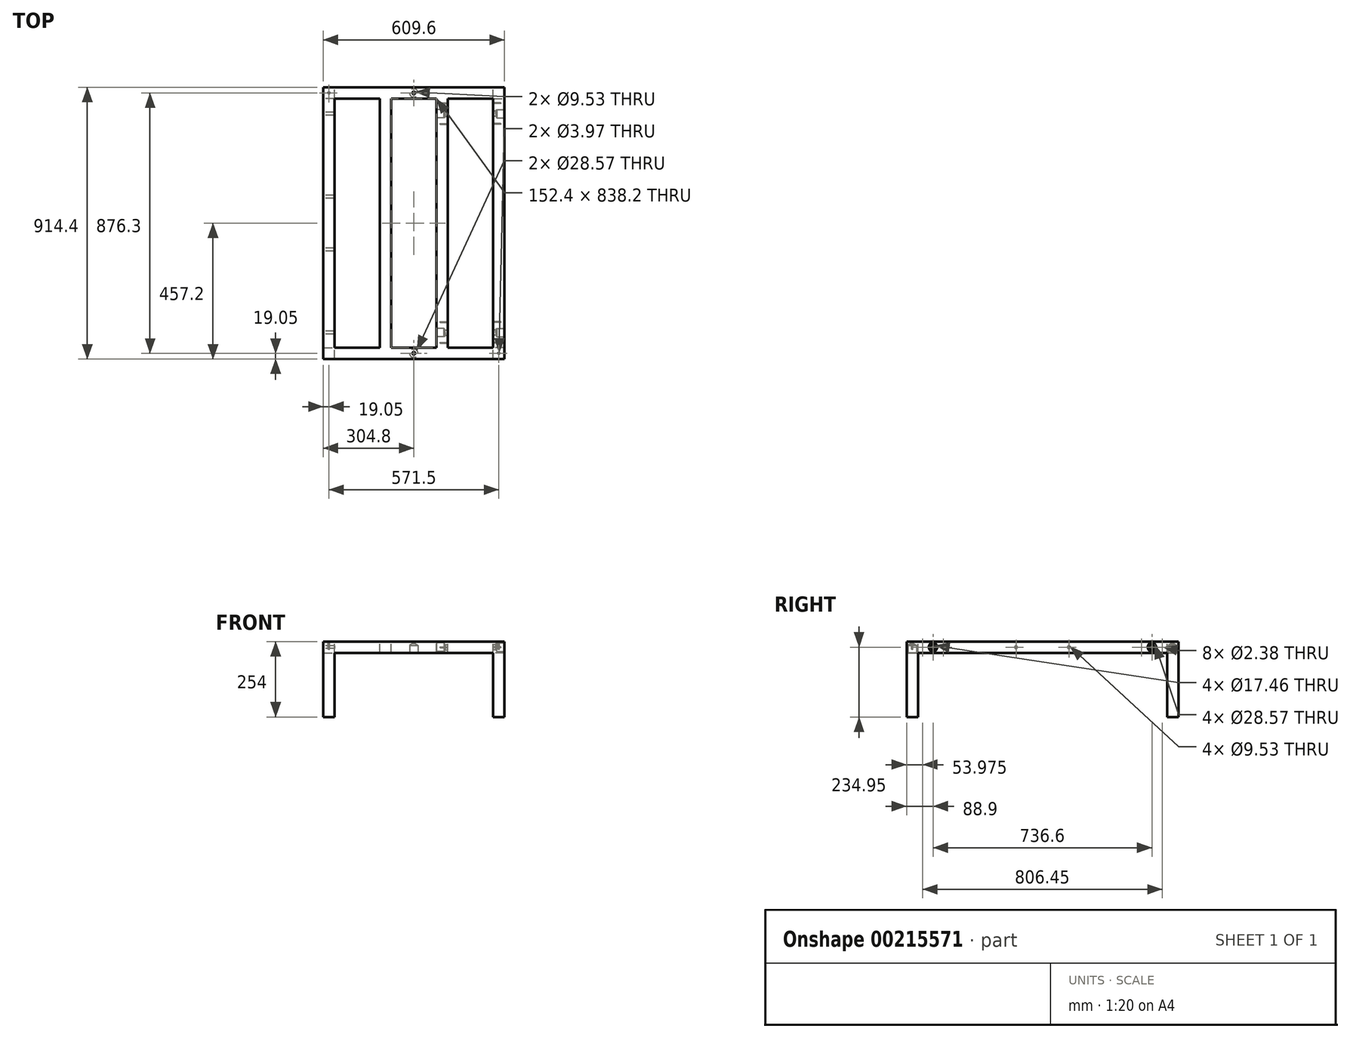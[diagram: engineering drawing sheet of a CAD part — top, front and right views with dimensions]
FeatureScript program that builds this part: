
annotation { "Feature Type Name" : "Feature", "Feature Type Description" : "" }
export const myFeature = defineFeature(function(context is Context, id is Id, definition is map)
    precondition{}
    {
        {
            var Q0;
            Q0=qCreatedBy(makeId("Top.planeOp"),FACE);
            var sketch = newSketch(context, id + "F0", { "sketchPlane" : qUnion([Q0])});
            skLineSegment(sketch, "E0.bottom", {"start": v(304.8, 457.2) * mm, "end": v(-304.8, 457.2) * mm});
            skLineSegment(sketch, "E0.top", {"start": v(304.8, -457.2) * mm, "end": v(-304.8, -457.2) * mm});
            skLineSegment(sketch, "E0.left", {"start": v(304.8, 457.2) * mm, "end": v(304.8, -457.2) * mm});
            skLineSegment(sketch, "E0.right", {"start": v(-304.8, 457.2) * mm, "end": v(-304.8, -457.2) * mm});
            skPoint(sketch, "E0.middle", {"position": v(0, 0) * mm});
            skLineSegment(sketch, "E1.bottom", {"start": v(266.7, 419.1) * mm, "end": v(114.3, 419.1) * mm});
            skLineSegment(sketch, "E1.top", {"start": v(266.7, -419.1) * mm, "end": v(114.3, -419.1) * mm});
            skLineSegment(sketch, "E1.left", {"start": v(266.7, 419.1) * mm, "end": v(266.7, -419.1) * mm});
            skLineSegment(sketch, "E1.right", {"start": v(-266.7, 419.1) * mm, "end": v(-266.7, -419.1) * mm});
            skLineSegment(sketch, "E2.0", {"start": v(-114.3, 419.1) * mm, "end": v(-114.3, -419.1) * mm});
            skLineSegment(sketch, "E3.0", {"start": v(-76.2, 419.1) * mm, "end": v(-76.2, -419.1) * mm});
            skLineSegment(sketch, "E4.0", {"start": v(76.2, 419.1) * mm, "end": v(76.2, -419.1) * mm});
            skLineSegment(sketch, "E5.0", {"start": v(114.3, 419.1) * mm, "end": v(114.3, -419.1) * mm});
            skLineSegment(sketch, "E6.trimOffspring", {"start": v(-114.3, 419.1) * mm, "end": v(-266.7, 419.1) * mm});
            skLineSegment(sketch, "E7.trimOffspring", {"start": v(76.2, 419.1) * mm, "end": v(-76.2, 419.1) * mm});
            skLineSegment(sketch, "E8.trimOffspring", {"start": v(-114.3, -419.1) * mm, "end": v(-266.7, -419.1) * mm});
            skLineSegment(sketch, "E9.trimOffspring", {"start": v(76.2, -419.1) * mm, "end": v(-76.2, -419.1) * mm});
            skSolve(sketch);
        }
        {
            var Q0;
            Q0 = qSketchRegion(id + "F0", true);
            extrude(context, id + "F1", {"entities" : qUnion([Q0]), "oppositeDirection" : true, "depth" : 38.1 * mm});
        }
        {
            var Q0;
            Q0=makeQuery(id+"F1.opExtrude","CAP_FACE",FACE,{"disambiguationData":[OSD([sQuery(id+"F0.wireOp",EDGE,"E0.bottom"),sQuery(id+"F0.wireOp",EDGE,"E0.top"),sQuery(id+"F0.wireOp",EDGE,"E0.left"),sQuery(id+"F0.wireOp",EDGE,"E0.right"),sQuery(id+"F0.wireOp",EDGE,"E1.bottom"),sQuery(id+"F0.wireOp",EDGE,"E1.top"),sQuery(id+"F0.wireOp",EDGE,"E1.left"),sQuery(id+"F0.wireOp",EDGE,"E1.right"),sQuery(id+"F0.wireOp",EDGE,"E2.0"),sQuery(id+"F0.wireOp",EDGE,"E3.0"),sQuery(id+"F0.wireOp",EDGE,"E4.0"),sQuery(id+"F0.wireOp",EDGE,"E5.0"),sQuery(id+"F0.wireOp",EDGE,"E6.trimOffspring"),sQuery(id+"F0.wireOp",EDGE,"E7.trimOffspring"),sQuery(id+"F0.wireOp",EDGE,"E8.trimOffspring"),sQuery(id+"F0.wireOp",EDGE,"E9.trimOffspring")])],"isStart":false});
            var sketch = newSketch(context, id + "F2", { "sketchPlane" : qUnion([Q0])});
            skLineSegment(sketch, "E10.bottom", {"start": v(-266.7, -419.1) * mm, "end": v(-304.8, -419.1) * mm});
            skLineSegment(sketch, "E10.top", {"start": v(-266.7, -457.2) * mm, "end": v(-304.8, -457.2) * mm});
            skLineSegment(sketch, "E10.left", {"start": v(-266.7, -419.1) * mm, "end": v(-266.7, -457.2) * mm});
            skLineSegment(sketch, "E10.right", {"start": v(-304.8, -419.1) * mm, "end": v(-304.8, -457.2) * mm});
            skLineSegment(sketch, "E11.bottom", {"start": v(266.7, -419.1) * mm, "end": v(304.8, -419.1) * mm});
            skLineSegment(sketch, "E11.top", {"start": v(266.7, -457.2) * mm, "end": v(304.8, -457.2) * mm});
            skLineSegment(sketch, "E11.left", {"start": v(266.7, -419.1) * mm, "end": v(266.7, -457.2) * mm});
            skLineSegment(sketch, "E11.right", {"start": v(304.8, -419.1) * mm, "end": v(304.8, -457.2) * mm});
            skLineSegment(sketch, "E12.bottom", {"start": v(-304.8, 457.2) * mm, "end": v(-266.7, 457.2) * mm});
            skLineSegment(sketch, "E12.top", {"start": v(-304.8, 419.1) * mm, "end": v(-266.7, 419.1) * mm});
            skLineSegment(sketch, "E12.left", {"start": v(-304.8, 457.2) * mm, "end": v(-304.8, 419.1) * mm});
            skLineSegment(sketch, "E12.right", {"start": v(-266.7, 457.2) * mm, "end": v(-266.7, 419.1) * mm});
            skLineSegment(sketch, "E13.bottom", {"start": v(304.8, 457.2) * mm, "end": v(266.7, 457.2) * mm});
            skLineSegment(sketch, "E13.top", {"start": v(304.8, 419.1) * mm, "end": v(266.7, 419.1) * mm});
            skLineSegment(sketch, "E13.left", {"start": v(304.8, 457.2) * mm, "end": v(304.8, 419.1) * mm});
            skLineSegment(sketch, "E13.right", {"start": v(266.7, 457.2) * mm, "end": v(266.7, 419.1) * mm});
            skSolve(sketch);
        }
        {
            var Q0;
            Q0=makeQuery(id+"F2.imprint","IMPRINT",FACE,{"disambiguationData":[TD([[makeQuery(id+"F2.imprint","IMPRINT",EDGE,{"derivedFrom":sQuery(id+"F2.wireOp",EDGE,"E10.bottom")}),1.0]])]});
            var Q1;
            Q1=makeQuery(id+"F2.imprint","IMPRINT",FACE,{"disambiguationData":[TD([[makeQuery(id+"F2.imprint","IMPRINT",EDGE,{"derivedFrom":sQuery(id+"F2.wireOp",EDGE,"E11.bottom")}),-1.0]])]});
            var Q2;
            Q2=makeQuery(id+"F2.imprint","IMPRINT",FACE,{"disambiguationData":[TD([[makeQuery(id+"F2.imprint","IMPRINT",EDGE,{"derivedFrom":sQuery(id+"F2.wireOp",EDGE,"E13.bottom")}),1.0]])]});
            var Q3;
            Q3=makeQuery(id+"F2.imprint","IMPRINT",FACE,{"disambiguationData":[TD([[makeQuery(id+"F2.imprint","IMPRINT",EDGE,{"derivedFrom":sQuery(id+"F2.wireOp",EDGE,"E12.bottom")}),1.0]])]});
            extrude(context, id + "F3", {"entities" : qUnion([Q0, Q1, Q2, Q3]), "operationType" : NewBodyOperationType.ADD, "depth" : 215.9 * mm});
        }
        {
            var Q0;
            Q0=makeQuery(id+"F3.boolean.opBoolean","MERGE",FACE,{"derivedFrom":[makeQuery(id+"F1.opExtrude","SWEPT_FACE",FACE,{"disambiguationData":[OSD([sQuery(id+"F0.wireOp",EDGE,"E0.left")])]}),makeQuery(id+"F3.opExtrude","SWEPT_FACE",FACE,{"disambiguationData":[OSD([sQuery(id+"F2.wireOp",EDGE,"E11.right")])]}),makeQuery(id+"F3.opExtrude","SWEPT_FACE",FACE,{"disambiguationData":[OSD([sQuery(id+"F2.wireOp",EDGE,"E13.left")])]})]});
            var sketch = newSketch(context, id + "F4", { "sketchPlane" : qUnion([Q0])});
            skPoint(sketch, "E14", {"position": v(368.3, -19.05) * mm});
            skPoint(sketch, "E15", {"position": v(-368.3, -19.05) * mm});
            skPoint(sketch, "E16", {"position": v(-200.65, 261.37) * mm});
            skSolve(sketch);
        }
        {
            var Q0;
            Q0=makeQuery(id+"F1.opExtrude","SWEPT_FACE",FACE,{"disambiguationData":[OSD([sQuery(id+"F0.wireOp",EDGE,"E5.0")])]});
            var sketch = newSketch(context, id + "F5", { "sketchPlane" : qUnion([Q0])});
            skPoint(sketch, "E17.0", {"position": v(368.3, -19.05) * mm});
            skPoint(sketch, "E18.0", {"position": v(-368.3, -19.05) * mm});
            skSolve(sketch);
        }
        {
            var Q0;
            Q0=makeQuery(id+"F3.boolean.opBoolean","MERGE",FACE,{"derivedFrom":[makeQuery(id+"F1.opExtrude","SWEPT_FACE",FACE,{"disambiguationData":[OSD([sQuery(id+"F0.wireOp",EDGE,"E0.right")])]}),makeQuery(id+"F3.opExtrude","SWEPT_FACE",FACE,{"disambiguationData":[OSD([sQuery(id+"F2.wireOp",EDGE,"E10.right")])]}),makeQuery(id+"F3.opExtrude","SWEPT_FACE",FACE,{"disambiguationData":[OSD([sQuery(id+"F2.wireOp",EDGE,"E12.left")])]})]});
            var sketch = newSketch(context, id + "F6", { "sketchPlane" : qUnion([Q0])});
            skPoint(sketch, "E19.0", {"position": v(-368.3, -19.05) * mm});
            skPoint(sketch, "E20.0", {"position": v(-88.9, -19.05) * mm});
            skPoint(sketch, "E21.0", {"position": v(88.9, -19.05) * mm});
            skPoint(sketch, "E22.0", {"position": v(368.3, -19.05) * mm});
            skSolve(sketch);
        }
        {
            var Q0;
            Q0=makeQuery(id+"F1.opExtrude","SWEPT_FACE",FACE,{"disambiguationData":[OSD([sQuery(id+"F0.wireOp",EDGE,"E1.left")])]});
            var sketch = newSketch(context, id + "F7", { "sketchPlane" : qUnion([Q0])});
            skPoint(sketch, "E23.0", {"position": v(-368.3, -19.05) * mm});
            skPoint(sketch, "E24.0", {"position": v(368.3, -19.05) * mm});
            skPoint(sketch, "E25", {"position": v(403.23, -19.05) * mm});
            skPoint(sketch, "E26", {"position": v(333.38, -19.05) * mm});
            skLineSegment(sketch, "E27", {"start": v(368.3, -19.05) * mm, "end": v(368.3, 30.08) * mm, "construction": true});
            skPoint(sketch, "E28", {"position": v(-333.38, -19.05) * mm});
            skPoint(sketch, "E29", {"position": v(-403.23, -19.05) * mm});
            skLineSegment(sketch, "E30", {"start": v(-368.3, -19.05) * mm, "end": v(-368.3, 29.6) * mm, "construction": true});
            skSolve(sketch);
        }
        {
            var Q0;
            Q0=sQuery(id+"F4.wireOp",VERTEX,"E14");
            var Q1;
            Q1=sQuery(id+"F4.wireOp",VERTEX,"E15");
            var Q2;
            Q2=makeQuery(id+"F1.opExtrude","SWEPT_BODY",BODY,{"disambiguationData":[OSD([sQuery(id+"F0.wireOp",EDGE,"E0.bottom"),sQuery(id+"F0.wireOp",EDGE,"E0.top"),sQuery(id+"F0.wireOp",EDGE,"E0.left"),sQuery(id+"F0.wireOp",EDGE,"E0.right"),sQuery(id+"F0.wireOp",EDGE,"E1.bottom"),sQuery(id+"F0.wireOp",EDGE,"E1.top"),sQuery(id+"F0.wireOp",EDGE,"E1.left"),sQuery(id+"F0.wireOp",EDGE,"E1.right"),sQuery(id+"F0.wireOp",EDGE,"E2.0"),sQuery(id+"F0.wireOp",EDGE,"E3.0"),sQuery(id+"F0.wireOp",EDGE,"E4.0"),sQuery(id+"F0.wireOp",EDGE,"E5.0"),sQuery(id+"F0.wireOp",EDGE,"E6.trimOffspring"),sQuery(id+"F0.wireOp",EDGE,"E7.trimOffspring"),sQuery(id+"F0.wireOp",EDGE,"E8.trimOffspring"),sQuery(id+"F0.wireOp",EDGE,"E9.trimOffspring")])]});
            hole(context, id + "F8", {"style" : HoleStyle.SIMPLE, "endStyle" : HoleEndStyle.BLIND, "holeDiameter" : 28.57 * mm, "holeDepth" : 25.4 * mm, "locations" : qUnion([Q0, Q1]), "scope" : qUnion([Q2])});
        }
        {
            var Q0;
            Q0=sQuery(id+"F5.wireOp",VERTEX,"E17.0");
            var Q1;
            Q1=sQuery(id+"F5.wireOp",VERTEX,"E18.0");
            var Q2;
            Q2=makeQuery(id+"F1.opExtrude","SWEPT_BODY",BODY,{"disambiguationData":[OSD([sQuery(id+"F0.wireOp",EDGE,"E0.bottom"),sQuery(id+"F0.wireOp",EDGE,"E0.top"),sQuery(id+"F0.wireOp",EDGE,"E0.left"),sQuery(id+"F0.wireOp",EDGE,"E0.right"),sQuery(id+"F0.wireOp",EDGE,"E1.bottom"),sQuery(id+"F0.wireOp",EDGE,"E1.top"),sQuery(id+"F0.wireOp",EDGE,"E1.left"),sQuery(id+"F0.wireOp",EDGE,"E1.right"),sQuery(id+"F0.wireOp",EDGE,"E2.0"),sQuery(id+"F0.wireOp",EDGE,"E3.0"),sQuery(id+"F0.wireOp",EDGE,"E4.0"),sQuery(id+"F0.wireOp",EDGE,"E5.0"),sQuery(id+"F0.wireOp",EDGE,"E6.trimOffspring"),sQuery(id+"F0.wireOp",EDGE,"E7.trimOffspring"),sQuery(id+"F0.wireOp",EDGE,"E8.trimOffspring"),sQuery(id+"F0.wireOp",EDGE,"E9.trimOffspring")])]});
            hole(context, id + "F9", {"style" : HoleStyle.SIMPLE, "endStyle" : HoleEndStyle.BLIND, "holeDiameter" : 17.46 * mm, "holeDepth" : 25.4 * mm, "locations" : qUnion([Q0, Q1]), "scope" : qUnion([Q2])});
        }
        {
            var Q0;
            Q0=sQuery(id+"F7.wireOp",VERTEX,"E23.0");
            var Q1;
            Q1=sQuery(id+"F7.wireOp",VERTEX,"E24.0");
            var Q2;
            Q2=makeQuery(id+"F1.opExtrude","SWEPT_BODY",BODY,{"disambiguationData":[OSD([sQuery(id+"F0.wireOp",EDGE,"E0.bottom"),sQuery(id+"F0.wireOp",EDGE,"E0.top"),sQuery(id+"F0.wireOp",EDGE,"E0.left"),sQuery(id+"F0.wireOp",EDGE,"E0.right"),sQuery(id+"F0.wireOp",EDGE,"E1.bottom"),sQuery(id+"F0.wireOp",EDGE,"E1.top"),sQuery(id+"F0.wireOp",EDGE,"E1.left"),sQuery(id+"F0.wireOp",EDGE,"E1.right"),sQuery(id+"F0.wireOp",EDGE,"E2.0"),sQuery(id+"F0.wireOp",EDGE,"E3.0"),sQuery(id+"F0.wireOp",EDGE,"E4.0"),sQuery(id+"F0.wireOp",EDGE,"E5.0"),sQuery(id+"F0.wireOp",EDGE,"E6.trimOffspring"),sQuery(id+"F0.wireOp",EDGE,"E7.trimOffspring"),sQuery(id+"F0.wireOp",EDGE,"E8.trimOffspring"),sQuery(id+"F0.wireOp",EDGE,"E9.trimOffspring")])]});
            hole(context, id + "F10", {"style" : HoleStyle.SIMPLE, "endStyle" : HoleEndStyle.BLIND, "holeDiameter" : 17.46 * mm, "holeDepth" : 25.4 * mm, "locations" : qUnion([Q0, Q1]), "scope" : qUnion([Q2])});
        }
        {
            var Q0;
            Q0=makeQuery(id+"F1.opExtrude","SWEPT_FACE",FACE,{"disambiguationData":[OSD([sQuery(id+"F0.wireOp",EDGE,"E4.0")])]});
            var sketch = newSketch(context, id + "F11", { "sketchPlane" : qUnion([Q0])});
            skPoint(sketch, "E31.0", {"position": v(-368.3, -19.05) * mm});
            skPoint(sketch, "E32.0", {"position": v(368.3, -19.05) * mm});
            skSolve(sketch);
        }
        {
            var Q0;
            Q0=sQuery(id+"F11.wireOp",VERTEX,"E31.0");
            var Q1;
            Q1=sQuery(id+"F11.wireOp",VERTEX,"E32.0");
            var Q2;
            Q2=makeQuery(id+"F1.opExtrude","SWEPT_BODY",BODY,{"disambiguationData":[OSD([sQuery(id+"F0.wireOp",EDGE,"E0.bottom"),sQuery(id+"F0.wireOp",EDGE,"E0.top"),sQuery(id+"F0.wireOp",EDGE,"E0.left"),sQuery(id+"F0.wireOp",EDGE,"E0.right"),sQuery(id+"F0.wireOp",EDGE,"E1.bottom"),sQuery(id+"F0.wireOp",EDGE,"E1.top"),sQuery(id+"F0.wireOp",EDGE,"E1.left"),sQuery(id+"F0.wireOp",EDGE,"E1.right"),sQuery(id+"F0.wireOp",EDGE,"E2.0"),sQuery(id+"F0.wireOp",EDGE,"E3.0"),sQuery(id+"F0.wireOp",EDGE,"E4.0"),sQuery(id+"F0.wireOp",EDGE,"E5.0"),sQuery(id+"F0.wireOp",EDGE,"E6.trimOffspring"),sQuery(id+"F0.wireOp",EDGE,"E7.trimOffspring"),sQuery(id+"F0.wireOp",EDGE,"E8.trimOffspring"),sQuery(id+"F0.wireOp",EDGE,"E9.trimOffspring")])]});
            hole(context, id + "F12", {"style" : HoleStyle.SIMPLE, "endStyle" : HoleEndStyle.BLIND, "holeDiameter" : 28.57 * mm, "holeDepth" : 25.4 * mm, "locations" : qUnion([Q0, Q1]), "scope" : qUnion([Q2])});
        }
        {
            var Q0;
            Q0=sQuery(id+"F6.wireOp",VERTEX,"E19.0");
            var Q1;
            Q1=sQuery(id+"F6.wireOp",VERTEX,"E20.0");
            var Q2;
            Q2=sQuery(id+"F6.wireOp",VERTEX,"E21.0");
            var Q3;
            Q3=sQuery(id+"F6.wireOp",VERTEX,"E22.0");
            var Q4;
            Q4=makeQuery(id+"F1.opExtrude","SWEPT_BODY",BODY,{"disambiguationData":[OSD([sQuery(id+"F0.wireOp",EDGE,"E0.bottom"),sQuery(id+"F0.wireOp",EDGE,"E0.top"),sQuery(id+"F0.wireOp",EDGE,"E0.left"),sQuery(id+"F0.wireOp",EDGE,"E0.right"),sQuery(id+"F0.wireOp",EDGE,"E1.bottom"),sQuery(id+"F0.wireOp",EDGE,"E1.top"),sQuery(id+"F0.wireOp",EDGE,"E1.left"),sQuery(id+"F0.wireOp",EDGE,"E1.right"),sQuery(id+"F0.wireOp",EDGE,"E2.0"),sQuery(id+"F0.wireOp",EDGE,"E3.0"),sQuery(id+"F0.wireOp",EDGE,"E4.0"),sQuery(id+"F0.wireOp",EDGE,"E5.0"),sQuery(id+"F0.wireOp",EDGE,"E6.trimOffspring"),sQuery(id+"F0.wireOp",EDGE,"E7.trimOffspring"),sQuery(id+"F0.wireOp",EDGE,"E8.trimOffspring"),sQuery(id+"F0.wireOp",EDGE,"E9.trimOffspring")])]});
            hole(context, id + "F13", {"style" : HoleStyle.SIMPLE, "endStyle" : HoleEndStyle.BLIND, "holeDiameter" : 9.52 * mm, "holeDepth" : 50.8 * mm, "locations" : qUnion([Q0, Q1, Q2, Q3]), "scope" : qUnion([Q4])});
        }
        {
            var Q0;
            Q0=makeQuery(id+"F1.opExtrude","SWEPT_FACE",FACE,{"disambiguationData":[OSD([sQuery(id+"F0.wireOp",EDGE,"E5.0")])]});
            var sketch = newSketch(context, id + "F14", { "sketchPlane" : qUnion([Q0])});
            skPoint(sketch, "E33.0", {"position": v(-403.23, -19.05) * mm});
            skPoint(sketch, "E34.0", {"position": v(-333.38, -19.05) * mm});
            skPoint(sketch, "E35.0", {"position": v(333.38, -19.05) * mm});
            skPoint(sketch, "E36.0", {"position": v(403.23, -19.05) * mm});
            skSolve(sketch);
        }
        {
            var Q0;
            Q0=sQuery(id+"F14.wireOp",VERTEX,"E33.0");
            var Q1;
            Q1=sQuery(id+"F14.wireOp",VERTEX,"E34.0");
            var Q2;
            Q2=sQuery(id+"F14.wireOp",VERTEX,"E35.0");
            var Q3;
            Q3=sQuery(id+"F14.wireOp",VERTEX,"E36.0");
            var Q4;
            Q4=sQuery(id+"F7.wireOp",VERTEX,"E25");
            var Q5;
            Q5=sQuery(id+"F7.wireOp",VERTEX,"E26");
            var Q6;
            Q6=sQuery(id+"F7.wireOp",VERTEX,"E28");
            var Q7;
            Q7=sQuery(id+"F7.wireOp",VERTEX,"E29");
            var Q8;
            Q8=makeQuery(id+"F1.opExtrude","SWEPT_BODY",BODY,{"disambiguationData":[OSD([sQuery(id+"F0.wireOp",EDGE,"E0.bottom"),sQuery(id+"F0.wireOp",EDGE,"E0.top"),sQuery(id+"F0.wireOp",EDGE,"E0.left"),sQuery(id+"F0.wireOp",EDGE,"E0.right"),sQuery(id+"F0.wireOp",EDGE,"E1.bottom"),sQuery(id+"F0.wireOp",EDGE,"E1.top"),sQuery(id+"F0.wireOp",EDGE,"E1.left"),sQuery(id+"F0.wireOp",EDGE,"E1.right"),sQuery(id+"F0.wireOp",EDGE,"E2.0"),sQuery(id+"F0.wireOp",EDGE,"E3.0"),sQuery(id+"F0.wireOp",EDGE,"E4.0"),sQuery(id+"F0.wireOp",EDGE,"E5.0"),sQuery(id+"F0.wireOp",EDGE,"E6.trimOffspring"),sQuery(id+"F0.wireOp",EDGE,"E7.trimOffspring"),sQuery(id+"F0.wireOp",EDGE,"E8.trimOffspring"),sQuery(id+"F0.wireOp",EDGE,"E9.trimOffspring")])]});
            hole(context, id + "F15", {"style" : HoleStyle.SIMPLE, "endStyle" : HoleEndStyle.BLIND, "holeDiameter" : 2.38 * mm, "holeDepth" : 25.4 * mm, "locations" : qUnion([Q0, Q1, Q2, Q3, Q4, Q5, Q6, Q7]), "scope" : qUnion([Q8])});
        }
        {
            var Q0;
            Q0=makeQuery(id+"F1.opExtrude","CAP_FACE",FACE,{"disambiguationData":[OSD([sQuery(id+"F0.wireOp",EDGE,"E0.bottom"),sQuery(id+"F0.wireOp",EDGE,"E0.top"),sQuery(id+"F0.wireOp",EDGE,"E0.left"),sQuery(id+"F0.wireOp",EDGE,"E0.right"),sQuery(id+"F0.wireOp",EDGE,"E1.bottom"),sQuery(id+"F0.wireOp",EDGE,"E1.top"),sQuery(id+"F0.wireOp",EDGE,"E1.left"),sQuery(id+"F0.wireOp",EDGE,"E1.right"),sQuery(id+"F0.wireOp",EDGE,"E2.0"),sQuery(id+"F0.wireOp",EDGE,"E3.0"),sQuery(id+"F0.wireOp",EDGE,"E4.0"),sQuery(id+"F0.wireOp",EDGE,"E5.0"),sQuery(id+"F0.wireOp",EDGE,"E6.trimOffspring"),sQuery(id+"F0.wireOp",EDGE,"E7.trimOffspring"),sQuery(id+"F0.wireOp",EDGE,"E8.trimOffspring"),sQuery(id+"F0.wireOp",EDGE,"E9.trimOffspring")])],"isStart":true});
            var sketch = newSketch(context, id + "F16", { "sketchPlane" : qUnion([Q0])});
            skPoint(sketch, "E37", {"position": v(285.75, -438.15) * mm});
            skPoint(sketch, "E38", {"position": v(-285.75, 438.15) * mm});
            skPoint(sketch, "E39.positionSnap0", {"position": v(190.5, -419.1) * mm});
            skPoint(sketch, "E40.positionSnap0", {"position": v(190.5, 419.1) * mm});
            skPoint(sketch, "E41", {"position": v(0, -438.15) * mm});
            skPoint(sketch, "E41.positionSnap0", {"position": v(0, -419.1) * mm});
            skPoint(sketch, "E42", {"position": v(0, 438.15) * mm});
            skPoint(sketch, "E42.positionSnap0", {"position": v(0, 419.1) * mm});
            skSolve(sketch);
        }
        {
            var Q0;
            Q0=sQuery(id+"F16.wireOp",VERTEX,"E38");
            var Q1;
            Q1=sQuery(id+"F16.wireOp",VERTEX,"E37");
            var Q2;
            Q2=makeQuery(id+"F1.opExtrude","SWEPT_BODY",BODY,{"disambiguationData":[OSD([sQuery(id+"F0.wireOp",EDGE,"E0.bottom"),sQuery(id+"F0.wireOp",EDGE,"E0.top"),sQuery(id+"F0.wireOp",EDGE,"E0.left"),sQuery(id+"F0.wireOp",EDGE,"E0.right"),sQuery(id+"F0.wireOp",EDGE,"E1.bottom"),sQuery(id+"F0.wireOp",EDGE,"E1.top"),sQuery(id+"F0.wireOp",EDGE,"E1.left"),sQuery(id+"F0.wireOp",EDGE,"E1.right"),sQuery(id+"F0.wireOp",EDGE,"E2.0"),sQuery(id+"F0.wireOp",EDGE,"E3.0"),sQuery(id+"F0.wireOp",EDGE,"E4.0"),sQuery(id+"F0.wireOp",EDGE,"E5.0"),sQuery(id+"F0.wireOp",EDGE,"E6.trimOffspring"),sQuery(id+"F0.wireOp",EDGE,"E7.trimOffspring"),sQuery(id+"F0.wireOp",EDGE,"E8.trimOffspring"),sQuery(id+"F0.wireOp",EDGE,"E9.trimOffspring")])]});
            hole(context, id + "F17", {"style" : HoleStyle.SIMPLE, "endStyle" : HoleEndStyle.BLIND, "holeDiameter" : 3.97 * mm, "holeDepth" : 25.4 * mm, "locations" : qUnion([Q0, Q1]), "scope" : qUnion([Q2])});
        }
        {
            var Q0;
            Q0=sQuery(id+"F16.wireOp",VERTEX,"E42");
            var Q1;
            Q1=sQuery(id+"F16.wireOp",VERTEX,"E41");
            var Q2;
            Q2=makeQuery(id+"F1.opExtrude","SWEPT_BODY",BODY,{"disambiguationData":[OSD([sQuery(id+"F0.wireOp",EDGE,"E0.bottom"),sQuery(id+"F0.wireOp",EDGE,"E0.top"),sQuery(id+"F0.wireOp",EDGE,"E0.left"),sQuery(id+"F0.wireOp",EDGE,"E0.right"),sQuery(id+"F0.wireOp",EDGE,"E1.bottom"),sQuery(id+"F0.wireOp",EDGE,"E1.top"),sQuery(id+"F0.wireOp",EDGE,"E1.left"),sQuery(id+"F0.wireOp",EDGE,"E1.right"),sQuery(id+"F0.wireOp",EDGE,"E2.0"),sQuery(id+"F0.wireOp",EDGE,"E3.0"),sQuery(id+"F0.wireOp",EDGE,"E4.0"),sQuery(id+"F0.wireOp",EDGE,"E5.0"),sQuery(id+"F0.wireOp",EDGE,"E6.trimOffspring"),sQuery(id+"F0.wireOp",EDGE,"E7.trimOffspring"),sQuery(id+"F0.wireOp",EDGE,"E8.trimOffspring"),sQuery(id+"F0.wireOp",EDGE,"E9.trimOffspring")])]});
            hole(context, id + "F18", {"style" : HoleStyle.SIMPLE, "endStyle" : HoleEndStyle.BLIND, "holeDiameter" : 9.52 * mm, "holeDepth" : 25.4 * mm, "locations" : qUnion([Q0, Q1]), "scope" : qUnion([Q2])});
        }
        {
            var Q0;
            {var subQ0=sQuery(id+"F0.wireOp",EDGE,"E0.bottom");var subQ1=sQuery(id+"F0.wireOp",EDGE,"E0.top");var subQ2=sQuery(id+"F0.wireOp",EDGE,"E7.trimOffspring");var subQ3=sQuery(id+"F0.wireOp",EDGE,"E6.trimOffspring");var subQ4=sQuery(id+"F0.wireOp",EDGE,"E1.bottom");var subQ5=sQuery(id+"F0.wireOp",EDGE,"E9.trimOffspring");var subQ6=sQuery(id+"F0.wireOp",EDGE,"E2.0");var subQ7=sQuery(id+"F0.wireOp",EDGE,"E5.0");var subQ8=sQuery(id+"F0.wireOp",EDGE,"E8.trimOffspring");var subQ9=sQuery(id+"F0.wireOp",EDGE,"E4.0");var subQ10=sQuery(id+"F0.wireOp",EDGE,"E3.0");var subQ11=sQuery(id+"F0.wireOp",EDGE,"E1.right");var subQ12=sQuery(id+"F0.wireOp",EDGE,"E1.left");var subQ13=sQuery(id+"F0.wireOp",EDGE,"E1.top");var subQ14=makeQuery(id+"F1.opExtrude","CAP_FACE",FACE,{"disambiguationData":[OSD([subQ0,subQ1,sQuery(id+"F0.wireOp",EDGE,"E0.left"),sQuery(id+"F0.wireOp",EDGE,"E0.right"),subQ4,subQ13,subQ12,subQ11,subQ6,subQ10,subQ9,subQ7,subQ3,subQ2,subQ8,subQ5])],"isStart":false});Q0=makeQuery(id+"F3.boolean.opBoolean","SPLIT",FACE,{"disambiguationData":[TD([makeQuery(id+"F1.opExtrude","SWEPT_FACE",FACE,{"disambiguationData":[OSD([subQ0])]})])],"derivedFrom":subQ14});}
            var sketch = newSketch(context, id + "F19", { "sketchPlane" : qUnion([Q0])});
            skPoint(sketch, "E43.0", {"position": v(0, 438.15) * mm});
            skPoint(sketch, "E44.0", {"position": v(0, -438.15) * mm});
            skSolve(sketch);
        }
        {
            var Q0;
            Q0=sQuery(id+"F19.wireOp",VERTEX,"E43.0");
            var Q1;
            Q1=sQuery(id+"F19.wireOp",VERTEX,"E44.0");
            var Q2;
            Q2=makeQuery(id+"F1.opExtrude","SWEPT_BODY",BODY,{"disambiguationData":[OSD([sQuery(id+"F0.wireOp",EDGE,"E0.bottom"),sQuery(id+"F0.wireOp",EDGE,"E0.top"),sQuery(id+"F0.wireOp",EDGE,"E0.left"),sQuery(id+"F0.wireOp",EDGE,"E0.right"),sQuery(id+"F0.wireOp",EDGE,"E1.bottom"),sQuery(id+"F0.wireOp",EDGE,"E1.top"),sQuery(id+"F0.wireOp",EDGE,"E1.left"),sQuery(id+"F0.wireOp",EDGE,"E1.right"),sQuery(id+"F0.wireOp",EDGE,"E2.0"),sQuery(id+"F0.wireOp",EDGE,"E3.0"),sQuery(id+"F0.wireOp",EDGE,"E4.0"),sQuery(id+"F0.wireOp",EDGE,"E5.0"),sQuery(id+"F0.wireOp",EDGE,"E6.trimOffspring"),sQuery(id+"F0.wireOp",EDGE,"E7.trimOffspring"),sQuery(id+"F0.wireOp",EDGE,"E8.trimOffspring"),sQuery(id+"F0.wireOp",EDGE,"E9.trimOffspring")])]});
            hole(context, id + "F20", {"style" : HoleStyle.SIMPLE, "endStyle" : HoleEndStyle.BLIND, "holeDiameter" : 28.57 * mm, "holeDepth" : 25.4 * mm, "locations" : qUnion([Q0, Q1]), "scope" : qUnion([Q2])});
        }
        {
            var Q0;
            Q0=makeQuery(id+"F1.opExtrude","SWEPT_BODY",BODY,{"disambiguationData":[OSD([sQuery(id+"F0.wireOp",EDGE,"E0.bottom"),sQuery(id+"F0.wireOp",EDGE,"E0.top"),sQuery(id+"F0.wireOp",EDGE,"E0.left"),sQuery(id+"F0.wireOp",EDGE,"E0.right"),sQuery(id+"F0.wireOp",EDGE,"E1.bottom"),sQuery(id+"F0.wireOp",EDGE,"E1.top"),sQuery(id+"F0.wireOp",EDGE,"E1.left"),sQuery(id+"F0.wireOp",EDGE,"E1.right"),sQuery(id+"F0.wireOp",EDGE,"E2.0"),sQuery(id+"F0.wireOp",EDGE,"E3.0"),sQuery(id+"F0.wireOp",EDGE,"E4.0"),sQuery(id+"F0.wireOp",EDGE,"E5.0"),sQuery(id+"F0.wireOp",EDGE,"E6.trimOffspring"),sQuery(id+"F0.wireOp",EDGE,"E7.trimOffspring"),sQuery(id+"F0.wireOp",EDGE,"E8.trimOffspring"),sQuery(id+"F0.wireOp",EDGE,"E9.trimOffspring")])]});
            transform(context, id + "F21", {"entities" : qUnion([Q0]), "transformType" : TransformType.TRANSLATION_3D, "dx" : 0 * mm, "dy" : 0 * mm, "dz" : 0 * mm, "makeCopy" : true});
        }
        {
            var Q0;
            Q0=makeQuery(id+"F21.opPattern","COPY",BODY,{"derivedFrom":makeQuery(id+"F1.opExtrude","SWEPT_BODY",BODY,{"disambiguationData":[OSD([sQuery(id+"F0.wireOp",EDGE,"E0.bottom"),sQuery(id+"F0.wireOp",EDGE,"E0.top"),sQuery(id+"F0.wireOp",EDGE,"E0.left"),sQuery(id+"F0.wireOp",EDGE,"E0.right"),sQuery(id+"F0.wireOp",EDGE,"E1.bottom"),sQuery(id+"F0.wireOp",EDGE,"E1.top"),sQuery(id+"F0.wireOp",EDGE,"E1.left"),sQuery(id+"F0.wireOp",EDGE,"E1.right"),sQuery(id+"F0.wireOp",EDGE,"E2.0"),sQuery(id+"F0.wireOp",EDGE,"E3.0"),sQuery(id+"F0.wireOp",EDGE,"E4.0"),sQuery(id+"F0.wireOp",EDGE,"E5.0"),sQuery(id+"F0.wireOp",EDGE,"E6.trimOffspring"),sQuery(id+"F0.wireOp",EDGE,"E7.trimOffspring"),sQuery(id+"F0.wireOp",EDGE,"E8.trimOffspring"),sQuery(id+"F0.wireOp",EDGE,"E9.trimOffspring")])]}),"instanceName":"1"});
            deleteBodies(context, id + "F22", {"entities" : qUnion([Q0])});
        }
    });
